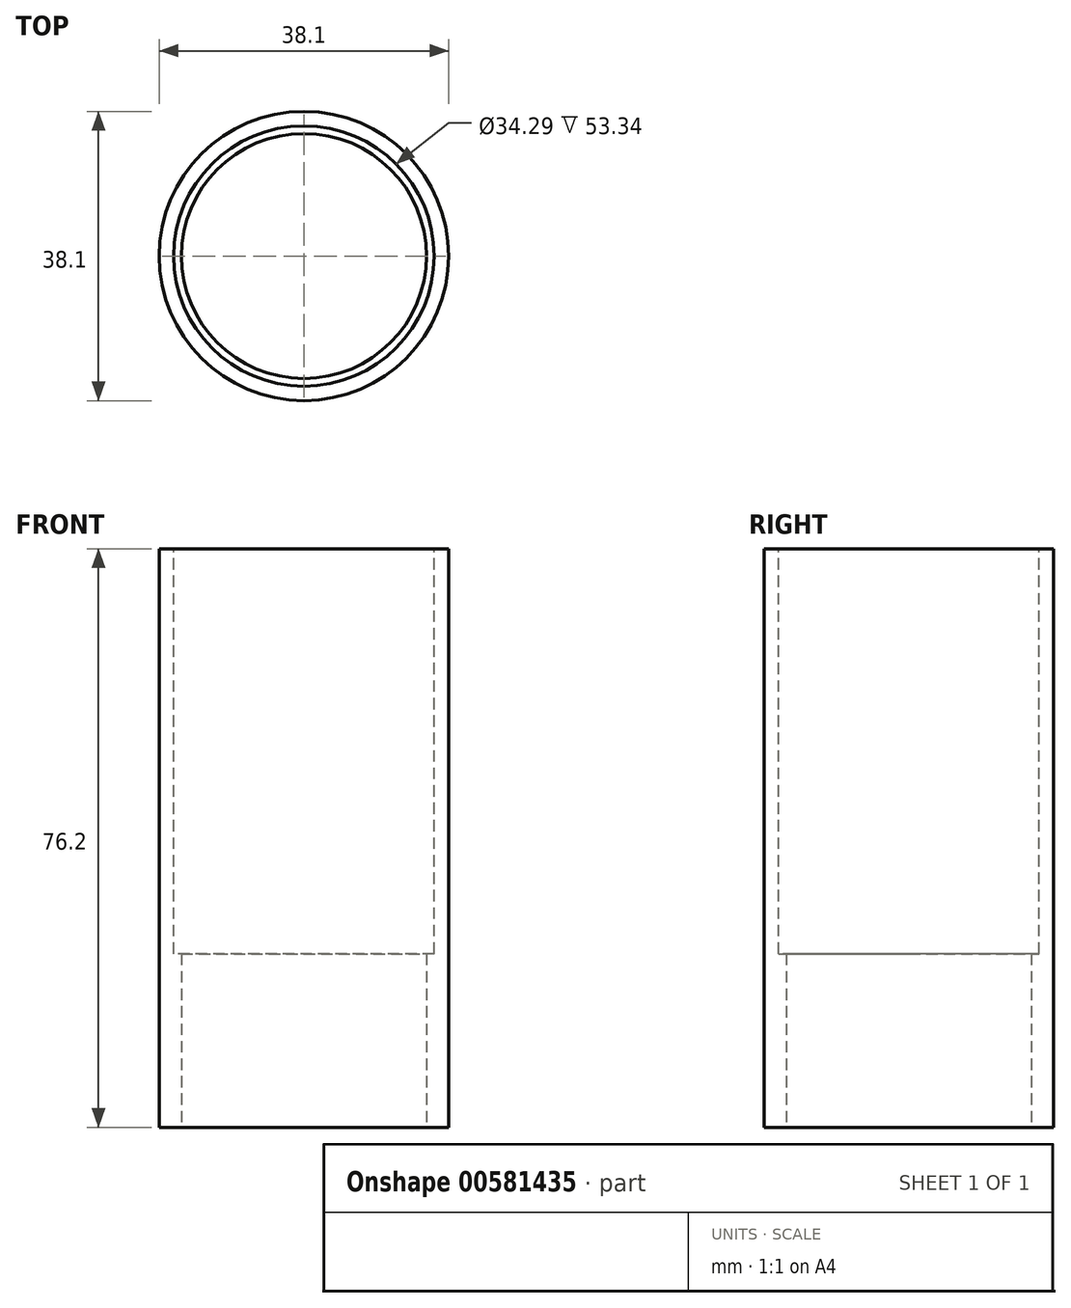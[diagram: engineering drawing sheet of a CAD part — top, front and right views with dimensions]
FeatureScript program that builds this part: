
annotation { "Feature Type Name" : "Feature", "Feature Type Description" : "" }
export const myFeature = defineFeature(function(context is Context, id is Id, definition is map)
    precondition{}
    {
        {
            var Q0;
            Q0=qCreatedBy(makeId("Top.planeOp"),FACE);
            var sketch = newSketch(context, id + "F0", { "sketchPlane" : qUnion([Q0])});
            skCircle(sketch, "E0", {"center": v(0, 0) * mm, "radius": 19.05 * mm});
            skSolve(sketch);
        }
        {
            var Q0;
            Q0=makeQuery(id+"F0.imprint","IMPRINT",FACE,{"disambiguationData":[TD([[makeQuery(id+"F0.imprint","IMPRINT",EDGE,{"derivedFrom":sQuery(id+"F0.wireOp",EDGE,"E0")}),1.0]])]});
            extrude(context, id + "F1", {"entities" : qUnion([Q0]), "depth" : 76.2 * mm, "offsetDistance" : 25.4 * mm, "symmetric" : true});
        }
        {
            var Q0;
            Q0=makeQuery(id+"F1.opExtrude","CAP_FACE",FACE,{"disambiguationData":[OSD([sQuery(id+"F0.wireOp",EDGE,"E0")])],"isStart":false});
            var sketch = newSketch(context, id + "F2", { "sketchPlane" : qUnion([Q0])});
            skPoint(sketch, "E1", {"position": v(0, 0) * mm});
            skSolve(sketch);
        }
        {
            var Q0;
            Q0=makeQuery(id+"F1.opExtrude","CAP_FACE",FACE,{"disambiguationData":[OSD([sQuery(id+"F0.wireOp",EDGE,"E0")])],"isStart":true});
            var sketch = newSketch(context, id + "F3", { "sketchPlane" : qUnion([Q0])});
            skCircle(sketch, "E2", {"center": v(0, 0) * mm, "radius": 16.13 * mm});
            skSolve(sketch);
        }
        {
            var Q0;
            Q0=makeQuery(id+"F3.imprint","IMPRINT",FACE,{"disambiguationData":[TD([[makeQuery(id+"F3.imprint","IMPRINT",EDGE,{"derivedFrom":sQuery(id+"F3.wireOp",EDGE,"E2")}),1.0]])]});
            extrude(context, id + "F4", {"entities" : qUnion([Q0]), "operationType" : NewBodyOperationType.REMOVE, "oppositeDirection" : true, "depth" : 22.86 * mm, "offsetDistance" : 25.4 * mm});
        }
        {
            var Q0;
            Q0=makeQuery(id+"F2.imprint","IMPRINT",FACE,{"disambiguationData":[TD([[makeQuery(id+"F2.imprint","IMPRINT",EDGE,{"derivedFrom":makeQuery(id+"F1.opExtrude","CAP_EDGE",EDGE,{"disambiguationData":[OSD([sQuery(id+"F0.wireOp",EDGE,"E0")])],"isStart":false})}),1.0]])]});
            var sketch = newSketch(context, id + "F5", { "sketchPlane" : qUnion([Q0])});
            skPoint(sketch, "E3", {"position": v(0, 0) * mm});
            skCircle(sketch, "E4", {"center": v(0, 0) * mm, "radius": 17.15 * mm});
            skSolve(sketch);
        }
        {
            var Q0;
            Q0=makeQuery(id+"F5.imprint","IMPRINT",FACE,{"disambiguationData":[TD([[makeQuery(id+"F5.imprint","IMPRINT",EDGE,{"derivedFrom":sQuery(id+"F5.wireOp",EDGE,"E4")}),1.0]])]});
            extrude(context, id + "F6", {"entities" : qUnion([Q0]), "operationType" : NewBodyOperationType.REMOVE, "oppositeDirection" : true, "depth" : 53.34 * mm, "offsetDistance" : 25.4 * mm});
        }
    });
